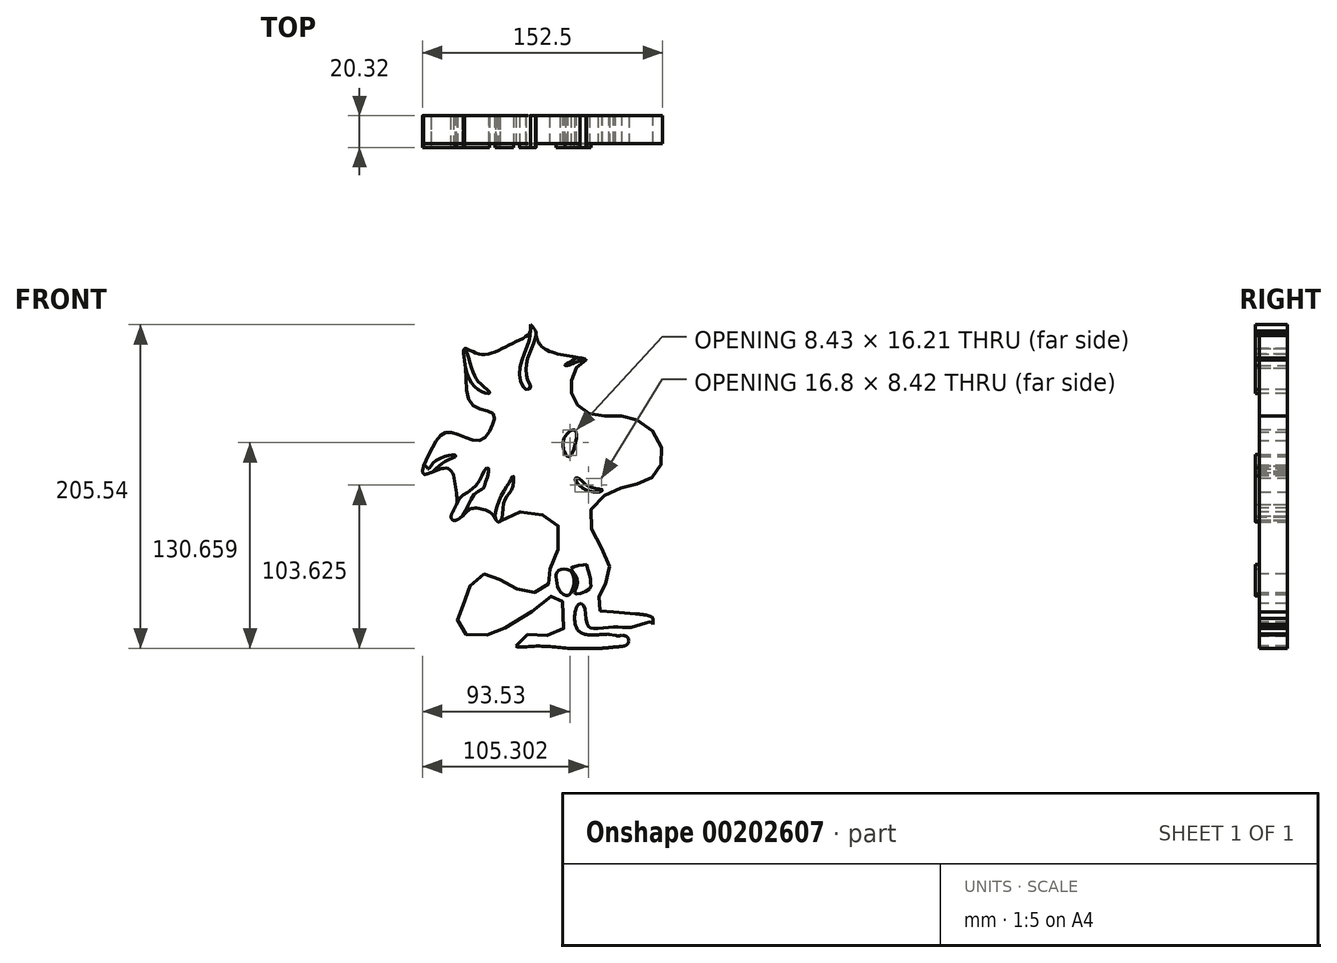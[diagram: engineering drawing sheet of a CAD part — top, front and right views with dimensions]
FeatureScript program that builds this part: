
annotation { "Feature Type Name" : "Feature", "Feature Type Description" : "" }
export const myFeature = defineFeature(function(context is Context, id is Id, definition is map)
    precondition{}
    {
        {
            var Q0;
            Q0=qCreatedBy(makeId("Front.planeOp"),FACE);
            var sketch = newSketch(context, id + "F0", { "sketchPlane" : qUnion([Q0])});
            skFitSpline(sketch, "E0", {"points": [v(59.54, 70.1) * mm, v(54.44, 66.24) * mm, v(50.73, 58.69) * mm, v(49.82, 51.76) * mm, v(51.57, 44.98) * mm, v(57.24, 38.47) * mm, v(65.28, 34.84) * mm, v(78.36, 34.49) * mm, v(89, 33.09) * mm, v(101.54, 25) * mm, v(108, 11.94) * mm, v(105.55, 0) * mm, v(97.34, -7.06) * mm, v(85.82, -10.2) * mm, v(73.94, -14.4) * mm, v(62.41, -25.55) * mm, v(65.2, -42.8) * mm, v(74.02, -59.29) * mm, v(71.53, -72.84) * mm, v(67.65, -80.3) * mm, v(68.48, -89.43) * mm, v(76.24, -89.98) * mm, v(89.53, -91.07) * mm, v(102, -94.1) * mm, v(100.62, -99.63) * mm, v(86.77, -103.79) * mm, v(81.78, -104.62) * mm, v(85.66, -106) * mm, v(85.94, -110.43) * mm, v(80.4, -112.09) * mm, v(64.6, -113.49) * mm, v(49.1, -113.23) * mm, v(25.82, -111.87) * mm, v(15.02, -111.6) * mm, v(20.28, -105.51) * mm, v(30.53, -104.12) * mm, v(43.28, -104.1) * mm, v(44.66, -83.37) * mm, v(39.4, -79.23) * mm, v(29.15, -86.7) * mm, v(4.5, -101.93) * mm, v(-5.48, -104.98) * mm, v(-19.33, -103.06) * mm, v(-22.1, -94.5) * mm, v(-19.33, -87.58) * mm, v(-15.46, -75.41) * mm, v(-6.6, -66.28) * mm, v(0, -67.38) * mm, v(11.41, -72.9) * mm, v(20.56, -77.59) * mm, v(31.36, -76.2) * mm, v(36.07, -70.94) * mm, v(36.62, -63.2) * mm, v(41.6, -50.47) * mm, v(40.77, -33.33) * mm, v(29.69, -27.81) * mm, v(13.35, -27.55) * mm, v(3.37, -32.82) * mm, v(0, -28.12) * mm, v(-12.7, -24.26) * mm, v(-17.68, -27.86) * mm, v(-24.33, -32.01) * mm, v(-26.27, -29.8) * mm, v(-22.94, -21.78) * mm, v(-22.94, -14.6) * mm, v(-26.55, 0) * mm, v(-35.41, 0) * mm, v(-43.72, -2.45) * mm, v(-43.72, 2.53) * mm, v(-38.74, 13.31) * mm, v(-31.26, 23.27) * mm, v(-21.29, 22.45) * mm, v(-8, 18.87) * mm, v(0, 28.56) * mm, v(0, 36.3) * mm, v(-12.7, 41.26) * mm, v(-17.14, 64.76) * mm, v(-17.7, 77.2) * mm, v(-8, 73.61) * mm, v(10.56, 79.44) * mm, v(24.16, 88.55) * mm, v(24.16, 92.42) * mm, v(27.48, 88.27) * mm, v(27.76, 86.34) * mm, v(33.85, 76.67) * mm, v(59.54, 70.1) * mm]});
            skFitSpline(sketch, "E1", {"points": [v(21.6, 51.2) * mm, v(17.06, 60.26) * mm, v(21.83, 78.16) * mm, v(24.16, 88.55) * mm, v(24.16, 92.42) * mm, v(27.48, 88.27) * mm, v(27.48, 84.56) * mm, v(24.16, 76.07) * mm, v(21.48, 66.19) * mm, v(22.65, 56.3) * mm, v(24.16, 52.7) * mm, v(21.6, 51.2) * mm]});
            skFitSpline(sketch, "E2", {"points": [v(-42.3, 2.53) * mm, v(-40.83, 0.72) * mm, v(-37.68, 4.46) * mm, v(-25.2, 9.82) * mm, v(-23.37, 9.01) * mm, v(-31.22, 4.83) * mm, v(-38.73, -1.37) * mm, v(-43.72, -2.45) * mm, v(-43.72, 2.53) * mm, v(-42.3, 2.53) * mm]});
            skFitSpline(sketch, "E3", {"points": [v(-22.94, -21.78) * mm, v(-19.41, -16.53) * mm, v(-9.9, -9.03) * mm, v(-4.32, 0.9) * mm, v(-2.4, 1) * mm, v(-4.67, -8.68) * mm, v(-5.8, -11.46) * mm, v(-11.47, -15.39) * mm, v(-18.92, -29.04) * mm, v(-24.33, -32.01) * mm, v(-26.27, -29.8) * mm, v(-22.94, -21.78) * mm]});
            skFitSpline(sketch, "E4", {"points": [v(47.3, 23.12) * mm, v(44.98, 14.05) * mm, v(48.94, 8.7) * mm, v(52.9, 24.98) * mm, v(47.3, 23.12) * mm]});
            skFitSpline(sketch, "E5", {"points": [v(68.02, -13.7) * mm, v(56.58, -10.93) * mm, v(52.61, -5.23) * mm, v(55.1, -5.52) * mm, v(61.42, -10.5) * mm, v(69.78, -12.53) * mm, v(68.02, -13.7) * mm]});
            skFitSpline(sketch, "E6", {"points": [v(48.18, -79.5) * mm, v(42.85, -76.92) * mm, v(40.43, -68.3) * mm, v(41.58, -64.03) * mm, v(48.34, -63.2) * mm, v(51.8, -69.45) * mm, v(48.18, -79.5) * mm]});
            skFitSpline(sketch, "E7", {"points": [v(49.83, -62.48) * mm, v(52.96, -66.7) * mm, v(53.57, -73.67) * mm, v(52.03, -77.84) * mm, v(53.62, -78.72) * mm, v(61.7, -75.25) * mm, v(62.42, -71.52) * mm, v(61.48, -65.76) * mm, v(60.1, -61.7) * mm, v(60, -60.11) * mm, v(56.7, -60.28) * mm, v(49.83, -62.48) * mm]});
            skLineSegment(sketch, "E8", {"start": v(54.57, -85.24) * mm, "end": v(54.57, -101.96) * mm});
            skLineSegment(sketch, "E9", {"start": v(54.57, -101.96) * mm, "end": v(73.97, -104.19) * mm});
            skLineSegment(sketch, "E10", {"start": v(73.97, -104.19) * mm, "end": v(79.55, -105.26) * mm});
            skLineSegment(sketch, "E11", {"start": v(79.55, -105.26) * mm, "end": v(84.81, -104.04) * mm});
            skLineSegment(sketch, "E12", {"start": v(84.81, -104.04) * mm, "end": v(99.27, -100.6) * mm});
            skLineSegment(sketch, "E13", {"start": v(99.27, -100.6) * mm, "end": v(101.94, -98.01) * mm});
            skLineSegment(sketch, "E14", {"start": v(101.94, -98.01) * mm, "end": v(102, -94.1) * mm});
            skLineSegment(sketch, "E15", {"start": v(90.73, -91.2) * mm, "end": v(77.01, -89.94) * mm});
            skLineSegment(sketch, "E16", {"start": v(77.01, -89.94) * mm, "end": v(69.85, -91.07) * mm});
            skPoint(sketch, "E17.10.internal.snap0", {"position": v(64.27, -103.07) * mm});
            skFitSpline(sketch, "E17", {"points": [v(54.57, -85.24) * mm, v(54.57, -101.96) * mm, v(73.97, -104.19) * mm, v(79.55, -105.26) * mm, v(84.81, -104.04) * mm, v(99.27, -100.6) * mm, v(101.94, -98.01) * mm, v(100.62, -96.5) * mm, v(88.81, -99.63) * mm, v(77.8, -99.63) * mm, v(64.27, -100.6) * mm, v(60.2, -98.01) * mm, v(58, -86.44) * mm, v(54.57, -85.24) * mm]});
            skFitSpline(sketch, "E18", {"points": [v(-17.7, 77.2) * mm, v(-17.14, 64.76) * mm, v(-7.29, 49.97) * mm, v(-1.72, 49.18) * mm, v(-7.9, 55.1) * mm, v(-13.04, 64.76) * mm, v(-17.7, 77.2) * mm]});
            skFitSpline(sketch, "E19", {"points": [v(2.3, -31.85) * mm, v(4.86, -17.74) * mm, v(12.02, -5.44) * mm, v(13.19, -3.76) * mm, v(12.69, -11.42) * mm, v(7.34, -19.84) * mm, v(5.22, -32.33) * mm, v(2.3, -31.85) * mm]});
            skFitSpline(sketch, "E20", {"points": [v(59.54, 70.1) * mm, v(55.56, 71.34) * mm, v(51.31, 70.1) * mm, v(46.02, 66.5) * mm, v(49.95, 67.18) * mm, v(55, 69.23) * mm, v(59.54, 70.1) * mm]});
            skLineSegment(sketch, "E21.bottom", {"start": v(84.08, -111.6) * mm, "end": v(85.77, -111.6) * mm});
            skLineSegment(sketch, "E21.top", {"start": v(15.02, -113.12) * mm, "end": v(69.53, -113.12) * mm});
            skLineSegment(sketch, "E21.left", {"start": v(15.02, -111.6) * mm, "end": v(15.02, -113.12) * mm});
            skSolve(sketch);
        }
        {
            var Q0;
            Q0=makeQuery(id+"F0.imprint","IMPRINT",FACE,{"disambiguationData":[TD([[makeQuery(id+"F0.imprint","IMPRINT",EDGE,{"derivedFrom":sQuery(id+"F0.wireOp",EDGE,"E4")}),-1.0]])]});
            extrude(context, id + "F1", {"entities" : qUnion([Q0]), "depth" : 17.78 * mm});
        }
        {
            var Q0;
            Q0=makeQuery(id+"F0.imprint","IMPRINT",FACE,{"disambiguationData":[TD([[makeQuery(id+"F0.imprint","IMPRINT",EDGE,{"derivedFrom":sQuery(id+"F0.wireOp",EDGE,"E6")}),-1.0]])]});
            var Q1;
            Q1=makeQuery(id+"F0.imprint","IMPRINT",FACE,{"disambiguationData":[TD([[makeQuery(id+"F0.imprint","IMPRINT",EDGE,{"derivedFrom":sQuery(id+"F0.wireOp",EDGE,"E7")}),1.0]])]});
            extrude(context, id + "F2", {"entities" : qUnion([Q0, Q1]), "operationType" : NewBodyOperationType.ADD, "depth" : 20.32 * mm});
        }
        {
            var Q0;
            {var subQ0=sQuery(id+"F0.wireOp",EDGE,"E18");var subQ1=sQuery(id+"F0.wireOp",EDGE,"E0");var subQ2=makeQuery(id+"F0.imprint","INTERSECT",VERTEX,{"disambiguationData":[OD(0.0)],"derivedFrom":[subQ1,subQ0]});Q0=makeQuery(id+"F0.imprint","IMPRINT",FACE,{"disambiguationData":[TD([[makeQuery(id+"F0.imprint","IMPRINT",EDGE,{"disambiguationData":[TD([[subQ2,-1.0]])],"derivedFrom":subQ1}),-1.0]])]});}
            var Q1;
            {var subQ0=sQuery(id+"F0.wireOp",EDGE,"E1");var subQ1=sQuery(id+"F0.wireOp",EDGE,"E0");var subQ7=makeQuery(id+"F0.imprint","INTERSECT",VERTEX,{"disambiguationData":[OD(0.0)],"derivedFrom":[subQ1,subQ0]});Q1=makeQuery(id+"F0.imprint","IMPRINT",FACE,{"disambiguationData":[TD([[makeQuery(id+"F0.imprint","IMPRINT",EDGE,{"disambiguationData":[TD([[subQ7,-1.0]])],"derivedFrom":subQ1}),-1.0]])]});}
            var Q2;
            {var subQ0=sQuery(id+"F0.wireOp",EDGE,"E20");var subQ1=sQuery(id+"F0.wireOp",EDGE,"E0");var subQ2=makeQuery(id+"F0.imprint","INTERSECT",VERTEX,{"disambiguationData":[OD(0.0)],"derivedFrom":[subQ1,subQ0]});Q2=makeQuery(id+"F0.imprint","IMPRINT",FACE,{"disambiguationData":[TD([[makeQuery(id+"F0.imprint","IMPRINT",EDGE,{"disambiguationData":[TD([[subQ2,1.0]])],"derivedFrom":subQ1}),-1.0]])]});}
            var Q3;
            {var subQ0=sQuery(id+"F0.wireOp",EDGE,"E2");var subQ1=sQuery(id+"F0.wireOp",EDGE,"E0");var subQ2=makeQuery(id+"F0.imprint","INTERSECT",VERTEX,{"disambiguationData":[OD(0.0)],"derivedFrom":[subQ1,subQ0]});Q3=makeQuery(id+"F0.imprint","IMPRINT",FACE,{"disambiguationData":[TD([[makeQuery(id+"F0.imprint","IMPRINT",EDGE,{"disambiguationData":[TD([[subQ2,-1.0]])],"derivedFrom":subQ1}),-1.0]])]});}
            var Q4;
            {var subQ0=sQuery(id+"F0.wireOp",EDGE,"E3");var subQ1=sQuery(id+"F0.wireOp",EDGE,"E0");var subQ2=makeQuery(id+"F0.imprint","INTERSECT",VERTEX,{"disambiguationData":[OD(0.0)],"derivedFrom":[subQ1,subQ0]});Q4=makeQuery(id+"F0.imprint","IMPRINT",FACE,{"disambiguationData":[TD([[makeQuery(id+"F0.imprint","IMPRINT",EDGE,{"disambiguationData":[TD([[subQ2,-1.0]])],"derivedFrom":subQ1}),-1.0]])]});}
            var Q5;
            {var subQ0=sQuery(id+"F0.wireOp",EDGE,"E19");var subQ1=sQuery(id+"F0.wireOp",EDGE,"E0");var subQ2=makeQuery(id+"F0.imprint","INTERSECT",VERTEX,{"disambiguationData":[OD(0.0)],"derivedFrom":[subQ1,subQ0]});Q5=makeQuery(id+"F0.imprint","IMPRINT",FACE,{"disambiguationData":[TD([[makeQuery(id+"F0.imprint","IMPRINT",EDGE,{"disambiguationData":[TD([[subQ2,-1.0]])],"derivedFrom":subQ1}),-1.0]])]});}
            var Q6;
            Q6=sQuery(id+"F0.wireOp",EDGE,"E1");
            var Q7;
            Q7=sQuery(id+"F0.wireOp",EDGE,"E18");
            var Q8;
            Q8=sQuery(id+"F0.wireOp",EDGE,"E2");
            var Q9;
            Q9=sQuery(id+"F0.wireOp",EDGE,"E3");
            var Q10;
            Q10=sQuery(id+"F0.wireOp",EDGE,"E19");
            var Q11;
            Q11=sQuery(id+"F0.wireOp",EDGE,"E20");
            extrude(context, id + "F3", {"entities" : qUnion([Q0, Q1, Q2, Q3, Q4, Q5]), "surfaceEntities" : qUnion([Q6, Q7, Q8, Q9, Q10, Q11]), "depth" : 20.32 * mm});
        }
    });
